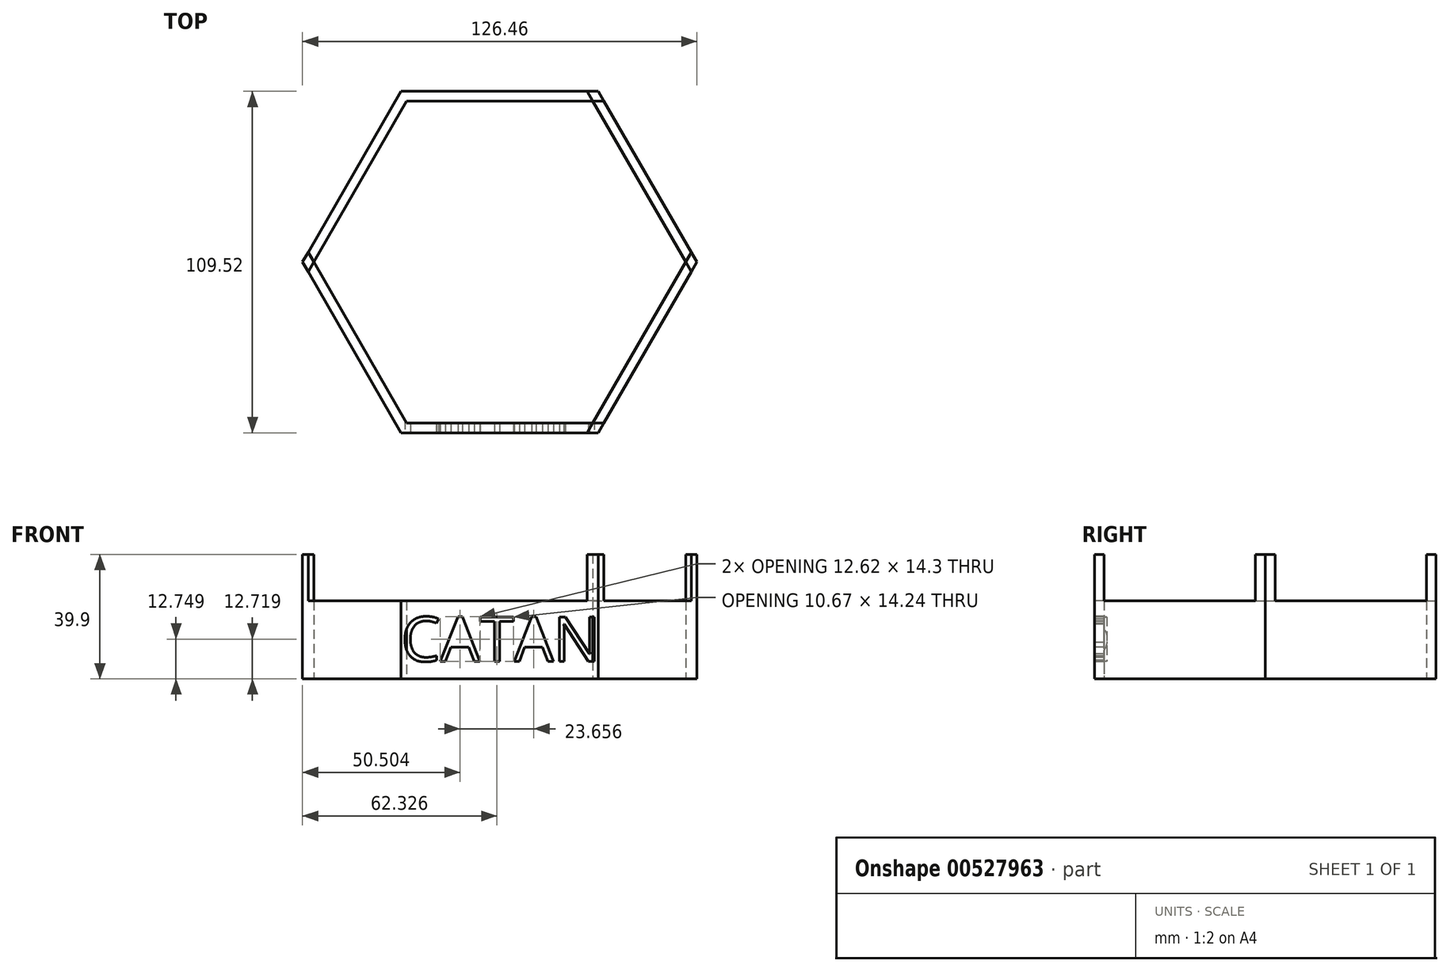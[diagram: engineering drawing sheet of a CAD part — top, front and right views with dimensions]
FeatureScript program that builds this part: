
annotation { "Feature Type Name" : "Feature", "Feature Type Description" : "" }
export const myFeature = defineFeature(function(context is Context, id is Id, definition is map)
    precondition{}
    {
        {
            var Q0;
            Q0=qCreatedBy(makeId("Top.planeOp"),FACE);
            var sketch = newSketch(context, id + "F0", { "sketchPlane" : qUnion([Q0])});
            skCircle(sketch, "E0.cCircle", {"center": v(0, 0) * mm, "radius": 54.76 * mm, "construction": true});
            skLineSegment(sketch, "E0.0", {"start": v(-31.62, 54.76) * mm, "end": v(31.62, 54.76) * mm});
            skLineSegment(sketch, "E0.1", {"start": v(31.62, 54.76) * mm, "end": v(63.23, 0) * mm});
            skLineSegment(sketch, "E0.2", {"start": v(63.23, 0) * mm, "end": v(31.62, -54.76) * mm});
            skLineSegment(sketch, "E0.3", {"start": v(31.62, -54.76) * mm, "end": v(-31.62, -54.76) * mm});
            skLineSegment(sketch, "E0.4", {"start": v(-31.62, -54.76) * mm, "end": v(-63.23, 0) * mm});
            skLineSegment(sketch, "E0.5", {"start": v(-63.23, 0) * mm, "end": v(-31.62, 54.76) * mm});
            skPoint(sketch, "E0.0.midPoint", {"position": v(0, 54.76) * mm});
            skCircle(sketch, "E1.cCircle", {"center": v(0, 0) * mm, "radius": 51.63 * mm, "construction": true});
            skLineSegment(sketch, "E1.0", {"start": v(-29.8, 51.63) * mm, "end": v(29.8, 51.63) * mm});
            skLineSegment(sketch, "E1.1", {"start": v(29.8, 51.63) * mm, "end": v(59.62, 0) * mm});
            skLineSegment(sketch, "E1.2", {"start": v(59.62, 0) * mm, "end": v(29.8, -51.63) * mm});
            skLineSegment(sketch, "E1.3", {"start": v(29.8, -51.63) * mm, "end": v(-29.8, -51.63) * mm});
            skLineSegment(sketch, "E1.4", {"start": v(-29.8, -51.63) * mm, "end": v(-59.62, 0) * mm});
            skLineSegment(sketch, "E1.5", {"start": v(-59.62, 0) * mm, "end": v(-29.8, 51.63) * mm});
            skPoint(sketch, "E1.0.midPoint", {"position": v(0, 51.63) * mm});
            skSolve(sketch);
        }
        {
            var Q0;
            Q0=makeQuery(id+"F0.imprint","IMPRINT",FACE,{"disambiguationData":[TD([[makeQuery(id+"F0.imprint","IMPRINT",EDGE,{"derivedFrom":sQuery(id+"F0.wireOp",EDGE,"E0.0")}),-1.0]])]});
            extrude(context, id + "F1", {"entities" : qUnion([Q0]), "depth" : 25 * mm, "offsetDistance" : 25 * mm});
        }
        {
            var Q0;
            Q0=makeQuery(id+"F1.opExtrude","CAP_FACE",FACE,{"disambiguationData":[OSD([sQuery(id+"F0.wireOp",EDGE,"E0.0"),sQuery(id+"F0.wireOp",EDGE,"E0.1"),sQuery(id+"F0.wireOp",EDGE,"E0.2"),sQuery(id+"F0.wireOp",EDGE,"E0.3"),sQuery(id+"F0.wireOp",EDGE,"E0.4"),sQuery(id+"F0.wireOp",EDGE,"E0.5"),sQuery(id+"F0.wireOp",EDGE,"E1.0"),sQuery(id+"F0.wireOp",EDGE,"E1.1"),sQuery(id+"F0.wireOp",EDGE,"E1.2"),sQuery(id+"F0.wireOp",EDGE,"E1.3"),sQuery(id+"F0.wireOp",EDGE,"E1.4"),sQuery(id+"F0.wireOp",EDGE,"E1.5")])],"isStart":false});
            var sketch = newSketch(context, id + "F2", { "sketchPlane" : qUnion([Q0])});
            skLineSegment(sketch, "E2", {"start": v(-29.8, 51.63) * mm, "end": v(-33.42, 51.63) * mm});
            skLineSegment(sketch, "E3", {"start": v(-33.42, 51.63) * mm, "end": v(33.42, 51.63) * mm});
            skLineSegment(sketch, "E4", {"start": v(29.8, 51.63) * mm, "end": v(28, 54.76) * mm});
            skLineSegment(sketch, "E5", {"start": v(28, 54.76) * mm, "end": v(61.42, -3.13) * mm});
            skLineSegment(sketch, "E6", {"start": v(59.62, 0) * mm, "end": v(61.42, 3.13) * mm});
            skLineSegment(sketch, "E7", {"start": v(61.42, 3.13) * mm, "end": v(29.8, -51.63) * mm});
            skLineSegment(sketch, "E8", {"start": v(29.8, -51.63) * mm, "end": v(28, -54.76) * mm});
            skLineSegment(sketch, "E9", {"start": v(29.8, -51.63) * mm, "end": v(33.42, -51.63) * mm});
            skLineSegment(sketch, "E10", {"start": v(33.42, -51.63) * mm, "end": v(-33.42, -51.63) * mm});
            skLineSegment(sketch, "E11", {"start": v(-33.42, -51.63) * mm, "end": v(-29.8, -51.63) * mm});
            skLineSegment(sketch, "E12", {"start": v(-59.62, 0) * mm, "end": v(-61.42, 3.13) * mm});
            skLineSegment(sketch, "E13", {"start": v(-61.42, 3.13) * mm, "end": v(-28, -54.76) * mm});
            skLineSegment(sketch, "E14", {"start": v(-59.62, 0) * mm, "end": v(-28, 54.76) * mm});
            skLineSegment(sketch, "E15", {"start": v(-59.62, 0) * mm, "end": v(-61.42, -3.13) * mm});
            skSolve(sketch);
        }
        {
            var Q0;
            {var subQ0=sQuery(id+"F2.wireOp",EDGE,"E15");Q0=makeQuery(id+"F2.imprint","IMPRINT",FACE,{"disambiguationData":[TD([[makeQuery(id+"F2.imprint","IMPRINT",EDGE,{"derivedFrom":subQ0}),-1.0]])]});}
            var Q1;
            {var subQ0=sQuery(id+"F2.wireOp",EDGE,"E14");var subQ1=sQuery(id+"F2.wireOp",EDGE,"E3");var subQ2=makeQuery(id+"F2.imprint","INTERSECT",VERTEX,{"derivedFrom":[subQ1,subQ0]});Q1=makeQuery(id+"F2.imprint","IMPRINT",FACE,{"disambiguationData":[TD([[makeQuery(id+"F2.imprint","IMPRINT",EDGE,{"disambiguationData":[TD([[subQ2,1.0]])],"derivedFrom":subQ1}),1.0]])]});}
            var Q2;
            {var subQ0=sQuery(id+"F2.wireOp",EDGE,"E5");var subQ1=sQuery(id+"F2.wireOp",EDGE,"E3");var subQ2=makeQuery(id+"F2.imprint","INTERSECT",VERTEX,{"derivedFrom":[subQ1,subQ0]});Q2=makeQuery(id+"F2.imprint","IMPRINT",FACE,{"disambiguationData":[TD([[makeQuery(id+"F2.imprint","IMPRINT",EDGE,{"disambiguationData":[TD([[subQ2,-1.0]])],"derivedFrom":subQ1}),1.0]])]});}
            var Q3;
            {var subQ0=sQuery(id+"F2.wireOp",EDGE,"E7");var subQ1=sQuery(id+"F2.wireOp",EDGE,"E5");var subQ2=makeQuery(id+"F2.imprint","INTERSECT",VERTEX,{"derivedFrom":[subQ1,subQ0]});Q3=makeQuery(id+"F2.imprint","IMPRINT",FACE,{"disambiguationData":[TD([[makeQuery(id+"F2.imprint","IMPRINT",EDGE,{"disambiguationData":[TD([[subQ2,-1.0]])],"derivedFrom":subQ1}),1.0]])]});}
            var Q4;
            {var subQ0=sQuery(id+"F2.wireOp",EDGE,"E8");Q4=makeQuery(id+"F2.imprint","IMPRINT",FACE,{"disambiguationData":[TD([[makeQuery(id+"F2.imprint","IMPRINT",EDGE,{"derivedFrom":subQ0}),1.0]])]});}
            var Q5;
            {var subQ0=sQuery(id+"F2.wireOp",EDGE,"E11");Q5=makeQuery(id+"F2.imprint","IMPRINT",FACE,{"disambiguationData":[TD([[makeQuery(id+"F2.imprint","IMPRINT",EDGE,{"derivedFrom":subQ0}),-1.0]])]});}
            extrude(context, id + "F3", {"entities" : qUnion([Q0, Q1, Q2, Q3, Q4, Q5]), "operationType" : NewBodyOperationType.ADD, "depth" : 14.9 * mm, "offsetDistance" : 25 * mm});
        }
        {
            var Q0;
            {var subQ0=sQuery(id+"F0.wireOp",EDGE,"E0.3");var subQ1=makeQuery(id+"F1.opExtrude","CAP_EDGE",EDGE,{"disambiguationData":[OSD([subQ0])],"isStart":false});Q0=makeQuery(id+"F3.boolean.opBoolean","MERGE",FACE,{"derivedFrom":[makeQuery(id+"F1.opExtrude","SWEPT_FACE",FACE,{"disambiguationData":[OSD([subQ0])]}),makeQuery(id+"F3.opExtrude","SWEPT_FACE",FACE,{"disambiguationData":[OSD([subQ0]),TDD([makeQuery(id+"F2.imprint","IMPRINT",EDGE,{"disambiguationData":[TD([[makeQuery(id+"F2.imprint","INTERSECT",VERTEX,{"derivedFrom":[makeQuery(id+"F1.opExtrude","CAP_EDGE",EDGE,{"disambiguationData":[OSD([sQuery(id+"F0.wireOp",EDGE,"E0.2")])],"isStart":false}),subQ1]}),-1.0]])],"derivedFrom":subQ1})])]}),makeQuery(id+"F3.opExtrude","SWEPT_FACE",FACE,{"disambiguationData":[OSD([subQ0]),TDD([makeQuery(id+"F2.imprint","IMPRINT",EDGE,{"disambiguationData":[TD([[makeQuery(id+"F2.imprint","INTERSECT",VERTEX,{"derivedFrom":[subQ1,makeQuery(id+"F1.opExtrude","CAP_EDGE",EDGE,{"disambiguationData":[OSD([sQuery(id+"F0.wireOp",EDGE,"E0.4")])],"isStart":false})]}),1.0]])],"derivedFrom":subQ1})])]})]});}
            var sketch = newSketch(context, id + "F4", { "sketchPlane" : qUnion([Q0])});
            skText(sketch, "E16", { "text": "CATAN\n", "fontName": "OpenSans-Regular.ttf"});
            const initialGuessF4  = {"E16": [-0.03162, 0.0056, 1, 0, 0.01436]};
            skSetInitialGuess(sketch, initialGuessF4);
            skSolve(sketch);
        }
        {
            var Q0;
            Q0 = qSketchRegion(id + "F4", true);
            var Q1;
            Q1=makeQuery(id+"F4.imprint","IMPRINT",FACE,{"disambiguationData":[TD([[makeQuery(id+"F4.imprint","IMPRINT",EDGE,{"derivedFrom":sQuery(id+"F4.wireOp",EDGE,"E16.sketch_text.stroke-23")}),1.0]])]});
            var Q2;
            Q2=makeQuery(id+"F4.imprint","IMPRINT",FACE,{"disambiguationData":[TD([[makeQuery(id+"F4.imprint","IMPRINT",EDGE,{"derivedFrom":sQuery(id+"F4.wireOp",EDGE,"E16.sketch_text.stroke-44")}),1.0]])]});
            extrude(context, id + "F5", {"entities" : qUnion([Q0, Q1, Q2]), "operationType" : NewBodyOperationType.REMOVE, "oppositeDirection" : true, "depth" : 25 * mm, "offsetDistance" : 25 * mm});
        }
    });
